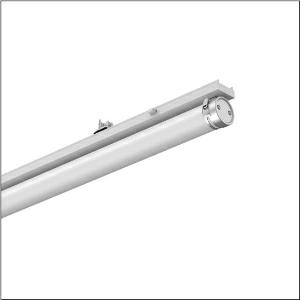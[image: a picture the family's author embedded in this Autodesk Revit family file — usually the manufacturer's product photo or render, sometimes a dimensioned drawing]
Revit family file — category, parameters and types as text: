
# Revit family: monsun_r__31_tube_51ft10mn4a0atr1_8ef5
name_source: partatom
category: Lighting Fixtures
units: mm (PartAtom-declared; Revit-internal decimal feet)

## family parameters
Cut with Voids When Loaded = No
Host = Face
Light Source = No
Part Type = Normal
Room Calculation Point = No
Round Connector Dimension = Use Diameter
Shared = No

## types (1)
- --- (1 x LED, 10000 lm, 58 W, 4000K)
    Apparent Load = 58 VA
    CIE Flux Codes = 42 71 90 91 100
    Color Rendering = 80
    Color Temperature = 4000K
    Default Elevation = 1800 mm
    Description = Monsun® 31 Tube, tubular luminaire, primary optical cover: diffuser, of PMMA, light emission: direct distribution, primary light characteristic: symmetric, LED, rated luminous flux: 10.000lm, luminous efficacy: 172lm/W, light colour: 840, colour temperature: 4000K, with with 1 terminal, 3-pole, max. 2.5mm², mains connection: 220..240V, AC, 50/60Hz, rated input power: 58W, housing, cylindrical, of PMMA, semi-transparent, matt white, with luminaire and ceiling fastening, V4A, mounting with brackets of stainless steel, length: 1.495mm, diameter: 75mm, end cap, of stainless steel (V4A), protection rating (complete): IP20, protection rating (lamp compartment): IP67/69K, insulation class (complete): insulation class I (protective earthing), certification: CE, UKCA, impact resistance: IK07, permissible operating ambient temperature: -20..+40°C, corresponds to IFS (International Featured Standards) requirements for safety and quality in the food industry, contact your sales advisor before using the luminaires in applications with unclear chemical exposure, large temperature fluctuations or condensation-forming humidity, packaging unit: 1 piece
    Height = 118 mm
    Lamp = 1 x LED
    Lamp Light Flux = 10000 lm
    Lamp Power = 58 W
    Lamp count = 1
    Length = 1495 mm
    Luminous efficacy = 172 lm/W
    Manufacturer = Siteco
    ModVariant = No
    Model = 51FT10MN4A0ATR1
    Mounting Place = Ceiling
    Mounting Type = Pendant
    Number of Poles = 1
    OnlyDefault = Yes
    Power Factor = 1
    Product Name = Monsun® 31 Tube
    Product group = tubular luminaire
    ProductGroupID = 906
    Protection Class = Protection class I
    Protection Degree = IP 20
    RLX_Detail_Level = 1
    RLX_Emergency_Light_Flux = 0 lm
    RLX_Emergency_Type = 0
    RLX_Emergency_Type_DB = No
    RlxData = <blob elided: 32281 chars, md5=fa52a5eb>
    Socket = socket
    Standby Power = 0 W
    System Light Flux = 10000 lm
    System Power = 58 W
    Type Comments = factory setting: luminous flux: 100 % | (OFF | OFF | OFF | OFF) | 350 mA
    Type Image = l_1007227.jpg
    URL = http://relux.com
    VarID = @adj_113181
    Voltage = 0 V
    Weight = 0.00 kg
    Width = 75 mm

## geometry (parser evidence)
native form markers: Blend x4, Sweep x12
no freeform markers — native parametric forms only
